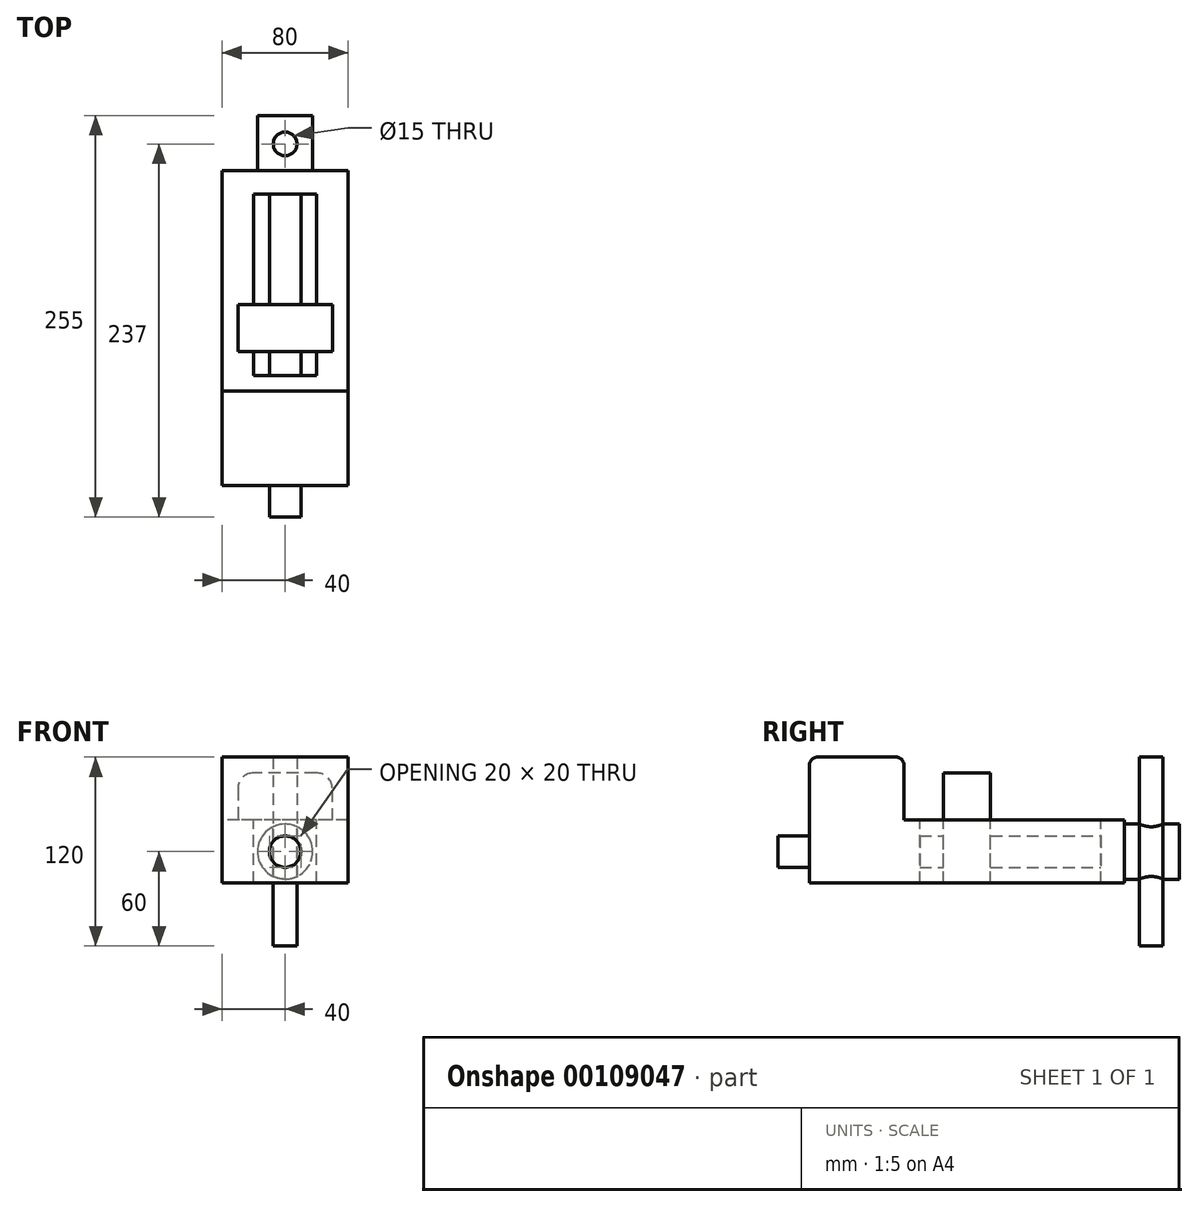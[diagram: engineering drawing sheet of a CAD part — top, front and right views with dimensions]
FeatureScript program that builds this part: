
annotation { "Feature Type Name" : "Feature", "Feature Type Description" : "" }
export const myFeature = defineFeature(function(context is Context, id is Id, definition is map)
    precondition{}
    {
        {
            var Q0;
            Q0=qCreatedBy(makeId("Right.planeOp"),FACE);
            var sketch = newSketch(context, id + "F0", { "sketchPlane" : qUnion([Q0])});
            skLineSegment(sketch, "E0", {"start": v(-100, 75) * mm, "end": v(-100, 0) * mm});
            skLineSegment(sketch, "E1", {"start": v(-100, 0) * mm, "end": v(100, 0) * mm});
            skLineSegment(sketch, "E2", {"start": v(100, 0) * mm, "end": v(100, 40) * mm});
            skLineSegment(sketch, "E3", {"start": v(100, 40) * mm, "end": v(-40, 40) * mm});
            skLineSegment(sketch, "E4", {"start": v(-40, 40) * mm, "end": v(-40, 75) * mm});
            skLineSegment(sketch, "E5", {"start": v(-45, 80) * mm, "end": v(-95, 80) * mm});
            skPoint(sketch, "E6.visualSharp", {"position": v(-40, 80) * mm});
            skArc(sketch, "E6.filletArc", {"start": v(-40, 75) * mm, "mid": v(-41.46, 78.54) * mm, "end": v(-45, 80) * mm});
            skPoint(sketch, "E7.visualSharp", {"position": v(-100, 80) * mm});
            skArc(sketch, "E7.filletArc", {"start": v(-95, 80) * mm, "mid": v(-98.54, 78.54) * mm, "end": v(-100, 75) * mm});
            skSolve(sketch);
        }
        {
            var Q0;
            Q0=makeQuery(id+"F0.imprint","IMPRINT",FACE,{"disambiguationData":[TD([[makeQuery(id+"F0.imprint","IMPRINT",EDGE,{"derivedFrom":sQuery(id+"F0.wireOp",EDGE,"E0")}),1.0]])]});
            extrude(context, id + "F1", {"entities" : qUnion([Q0]), "endBound" : BoundingType.SYMMETRIC, "depth" : 80 * mm});
        }
        {
            var Q0;
            Q0=makeQuery(id+"F1.opExtrude","SWEPT_FACE",FACE,{"disambiguationData":[OSD([sQuery(id+"F0.wireOp",EDGE,"E3")])]});
            var sketch = newSketch(context, id + "F2", { "sketchPlane" : qUnion([Q0])});
            skLineSegment(sketch, "E8.bottom", {"start": v(20, -30) * mm, "end": v(-20, -30) * mm});
            skLineSegment(sketch, "E8.top", {"start": v(20, 85) * mm, "end": v(-20, 85) * mm});
            skLineSegment(sketch, "E8.left", {"start": v(20, -30) * mm, "end": v(20, 85) * mm});
            skLineSegment(sketch, "E8.right", {"start": v(-20, -30) * mm, "end": v(-20, 85) * mm});
            skSolve(sketch);
        }
        {
            var Q0;
            Q0=makeQuery(id+"F2.imprint","IMPRINT",FACE,{"disambiguationData":[TD([[makeQuery(id+"F2.imprint","IMPRINT",EDGE,{"derivedFrom":sQuery(id+"F2.wireOp",EDGE,"E8.bottom")}),-1.0]])]});
            extrude(context, id + "F3", {"entities" : qUnion([Q0]), "operationType" : NewBodyOperationType.REMOVE, "endBound" : BoundingType.UP_TO_NEXT, "oppositeDirection" : true, "depth" : 25 * mm});
        }
        {
            var Q0;
            Q0=makeQuery(id+"F1.opExtrude","SWEPT_FACE",FACE,{"disambiguationData":[OSD([sQuery(id+"F0.wireOp",EDGE,"E2")])]});
            var sketch = newSketch(context, id + "F4", { "sketchPlane" : qUnion([Q0])});
            skCircle(sketch, "E9", {"center": v(0, 20) * mm, "radius": 10 * mm});
            skSolve(sketch);
        }
        {
            var Q0;
            Q0=makeQuery(id+"F4.imprint","IMPRINT",FACE,{"disambiguationData":[TD([[makeQuery(id+"F4.imprint","IMPRINT",EDGE,{"derivedFrom":sQuery(id+"F4.wireOp",EDGE,"E9")}),1.0]])]});
            extrude(context, id + "F5", {"entities" : qUnion([Q0]), "operationType" : NewBodyOperationType.REMOVE, "endBound" : BoundingType.THROUGH_ALL, "oppositeDirection" : true, "depth" : 25 * mm});
        }
        {
            var Q0;
            Q0=qCreatedBy(makeId("Front.planeOp"),FACE);
            var sketch = newSketch(context, id + "F6", { "sketchPlane" : qUnion([Q0])});
            skLineSegment(sketch, "E10.0", {"start": v(20, 0) * mm, "end": v(20, 40) * mm});
            skLineSegment(sketch, "E11.0", {"start": v(-20, 0) * mm, "end": v(-20, 40) * mm});
            skLineSegment(sketch, "E12.0", {"start": v(30, 40) * mm, "end": v(20, 40) * mm});
            skLineSegment(sketch, "E13.0", {"start": v(20, 0) * mm, "end": v(-20, 0) * mm});
            skLineSegment(sketch, "E14", {"start": v(30, 40) * mm, "end": v(30, 60) * mm});
            skLineSegment(sketch, "E15", {"start": v(20, 70) * mm, "end": v(-20, 70) * mm});
            skLineSegment(sketch, "E16", {"start": v(-30, 60) * mm, "end": v(-30, 40) * mm});
            skPoint(sketch, "E17.orphan", {"position": v(40, 40) * mm});
            skPoint(sketch, "E18.orphan", {"position": v(40, 0) * mm});
            skPoint(sketch, "E19.orphan", {"position": v(-40, 40) * mm});
            skLineSegment(sketch, "E20.trimOffspring", {"start": v(-20, 40) * mm, "end": v(-30, 40) * mm});
            skPoint(sketch, "E21.orphan", {"position": v(-40, 0) * mm});
            skPoint(sketch, "E22.visualSharp", {"position": v(30, 70) * mm});
            skArc(sketch, "E22.filletArc", {"start": v(30, 60) * mm, "mid": v(27.07, 67.07) * mm, "end": v(20, 70) * mm});
            skPoint(sketch, "E23.visualSharp", {"position": v(-30, 70) * mm});
            skArc(sketch, "E23.filletArc", {"start": v(-20, 70) * mm, "mid": v(-27.07, 67.07) * mm, "end": v(-30, 60) * mm});
            skCircle(sketch, "E24.0", {"center": v(0, 20) * mm, "radius": 10 * mm});
            skSolve(sketch);
        }
        {
            var Q0;
            Q0=makeQuery(id+"F6.imprint","IMPRINT",FACE,{"disambiguationData":[TD([[makeQuery(id+"F6.imprint","IMPRINT",EDGE,{"derivedFrom":sQuery(id+"F6.wireOp",EDGE,"E10.0")}),1.0]])]});
            extrude(context, id + "F7", {"entities" : qUnion([Q0]), "endBound" : BoundingType.SYMMETRIC, "depth" : 30 * mm});
        }
        {
            var Q0;
            Q0=makeQuery(id+"F1.opExtrude","SWEPT_FACE",FACE,{"disambiguationData":[OSD([sQuery(id+"F0.wireOp",EDGE,"E2")])]});
            var sketch = newSketch(context, id + "F8", { "sketchPlane" : qUnion([Q0])});
            skCircle(sketch, "E25.0", {"center": v(0, 20) * mm, "radius": 10 * mm});
            skCircle(sketch, "E26", {"center": v(0, 20) * mm, "radius": 17.5 * mm});
            skSolve(sketch);
        }
        {
            var Q0;
            Q0=makeQuery(id+"F8.imprint","IMPRINT",FACE,{"disambiguationData":[TD([[makeQuery(id+"F8.imprint","IMPRINT",EDGE,{"derivedFrom":sQuery(id+"F8.wireOp",EDGE,"E25.0")}),1.0]])]});
            var Q1;
            Q1=makeQuery(id+"F8.imprint","IMPRINT",FACE,{"disambiguationData":[TD([[makeQuery(id+"F8.imprint","IMPRINT",EDGE,{"derivedFrom":sQuery(id+"F8.wireOp",EDGE,"E25.0")}),-1.0]])]});
            extrude(context, id + "F9", {"entities" : qUnion([Q0, Q1]), "depth" : 35 * mm});
        }
        {
            var Q0;
            Q0=makeQuery(id+"F8.imprint","IMPRINT",FACE,{"disambiguationData":[TD([[makeQuery(id+"F8.imprint","IMPRINT",EDGE,{"derivedFrom":sQuery(id+"F8.wireOp",EDGE,"E25.0")}),1.0]])]});
            extrude(context, id + "F10", {"entities" : qUnion([Q0]), "operationType" : NewBodyOperationType.ADD, "oppositeDirection" : true, "depth" : 220 * mm});
        }
        {
            var Q0;
            Q0=makeQuery(id+"F1.opExtrude","SWEPT_FACE",FACE,{"disambiguationData":[OSD([sQuery(id+"F0.wireOp",EDGE,"E3")])]});
            var sketch = newSketch(context, id + "F11", { "sketchPlane" : qUnion([Q0])});
            skCircle(sketch, "E27", {"center": v(0, 117) * mm, "radius": 7.5 * mm});
            skSolve(sketch);
        }
        {
            var Q0;
            Q0=makeQuery(id+"F11.imprint","IMPRINT",FACE,{"disambiguationData":[TD([[makeQuery(id+"F11.imprint","IMPRINT",EDGE,{"derivedFrom":sQuery(id+"F11.wireOp",EDGE,"E27")}),1.0]])]});
            extrude(context, id + "F12", {"entities" : qUnion([Q0]), "operationType" : NewBodyOperationType.REMOVE, "endBound" : BoundingType.THROUGH_ALL, "oppositeDirection" : true, "depth" : 25 * mm});
        }
        {
            var Q0;
            Q0=makeQuery(id+"F1.opExtrude","SWEPT_FACE",FACE,{"disambiguationData":[OSD([sQuery(id+"F0.wireOp",EDGE,"E3")])]});
            var sketch = newSketch(context, id + "F13", { "sketchPlane" : qUnion([Q0])});
            skCircle(sketch, "E28.0", {"center": v(0, 117) * mm, "radius": 7.5 * mm});
            skSolve(sketch);
        }
        {
            var Q0;
            Q0=makeQuery(id+"F13.imprint","IMPRINT",FACE,{"disambiguationData":[TD([[makeQuery(id+"F13.imprint","IMPRINT",EDGE,{"derivedFrom":sQuery(id+"F13.wireOp",EDGE,"E28.0")}),1.0]])]});
            extrude(context, id + "F14", {"entities" : qUnion([Q0]), "depth" : 40 * mm, "hasSecondDirection" : true, "secondDirectionOppositeDirection" : true, "secondDirectionDepth" : 80 * mm});
        }
    });
